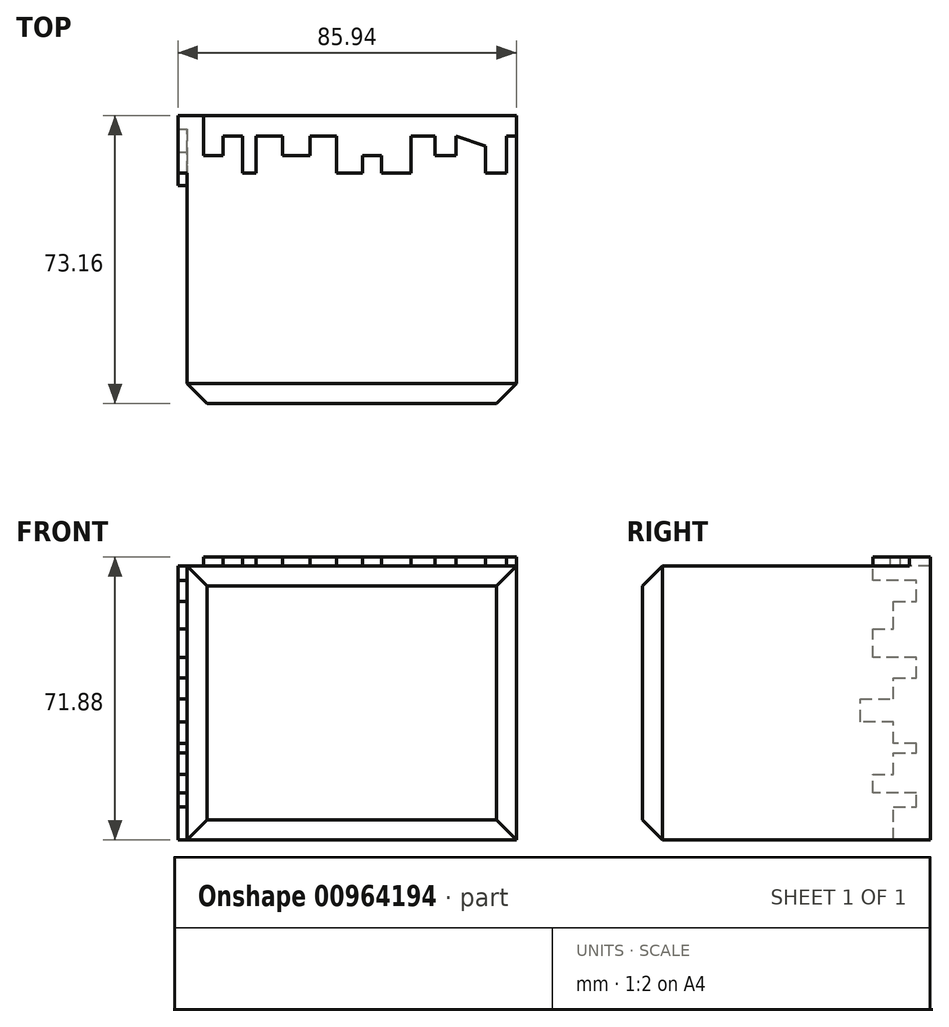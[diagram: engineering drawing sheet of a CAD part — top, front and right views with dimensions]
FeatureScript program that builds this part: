
annotation { "Feature Type Name" : "Feature", "Feature Type Description" : "" }
export const myFeature = defineFeature(function(context is Context, id is Id, definition is map)
    precondition{}
    {
        {
            var Q0;
            Q0=qCreatedBy(makeId("Top.planeOp"),FACE);
            var sketch = newSketch(context, id + "F0", { "sketchPlane" : qUnion([Q0])});
            skLineSegment(sketch, "E0.bottom", {"start": v(-44.6, 47.36) * mm, "end": v(39.06, 47.36) * mm});
            skLineSegment(sketch, "E0.top", {"start": v(-44.6, -25.8) * mm, "end": v(39.06, -25.8) * mm});
            skLineSegment(sketch, "E0.left", {"start": v(-44.6, 47.36) * mm, "end": v(-44.6, -25.8) * mm});
            skLineSegment(sketch, "E0.right", {"start": v(39.06, 47.36) * mm, "end": v(39.06, -25.8) * mm});
            skSolve(sketch);
        }
        {
            var Q0;
            Q0=makeQuery(id+"F0.imprint","IMPRINT",FACE,{"disambiguationData":[TD([[makeQuery(id+"F0.imprint","IMPRINT",EDGE,{"derivedFrom":sQuery(id+"F0.wireOp",EDGE,"E0.bottom")}),-1.0]])]});
            extrude(context, id + "F1", {"entities" : qUnion([Q0]), "depth" : 69.6 * mm});
        }
        {
            var Q0;
            Q0=makeQuery(id+"F1.opExtrude","SWEPT_FACE",FACE,{"disambiguationData":[OSD([sQuery(id+"F0.wireOp",EDGE,"E0.left")])]});
            var sketch = newSketch(context, id + "F2", { "sketchPlane" : qUnion([Q0])});
            skLineSegment(sketch, "E1", {"start": v(-38.04, 0) * mm, "end": v(-38.04, 8.45) * mm});
            skLineSegment(sketch, "E2", {"start": v(-38.04, 8.45) * mm, "end": v(-43.87, 8.45) * mm});
            skLineSegment(sketch, "E3", {"start": v(-43.87, 8.45) * mm, "end": v(-43.87, 11.95) * mm});
            skLineSegment(sketch, "E4", {"start": v(-43.87, 11.95) * mm, "end": v(-32.8, 11.95) * mm});
            skLineSegment(sketch, "E5", {"start": v(-32.8, 11.95) * mm, "end": v(-32.8, 16.61) * mm});
            skLineSegment(sketch, "E6", {"start": v(-32.8, 16.61) * mm, "end": v(-38.04, 16.61) * mm});
            skLineSegment(sketch, "E7", {"start": v(-38.04, 16.61) * mm, "end": v(-38.04, 22.15) * mm});
            skLineSegment(sketch, "E8", {"start": v(-38.04, 22.15) * mm, "end": v(-43.87, 22.15) * mm});
            skLineSegment(sketch, "E9", {"start": v(-43.87, 22.15) * mm, "end": v(-43.87, 24.48) * mm});
            skLineSegment(sketch, "E10", {"start": v(-43.87, 24.48) * mm, "end": v(-38.04, 24.48) * mm});
            skLineSegment(sketch, "E11", {"start": v(-38.04, 24.48) * mm, "end": v(-38.04, 30.02) * mm});
            skLineSegment(sketch, "E12", {"start": v(-38.04, 30.02) * mm, "end": v(-29.58, 30.02) * mm});
            skLineSegment(sketch, "E13", {"start": v(-29.58, 30.02) * mm, "end": v(-29.58, 35.85) * mm});
            skLineSegment(sketch, "E14", {"start": v(-29.58, 35.85) * mm, "end": v(-38.04, 35.85) * mm});
            skLineSegment(sketch, "E15", {"start": v(-38.04, 35.85) * mm, "end": v(-38.04, 41.1) * mm});
            skLineSegment(sketch, "E16", {"start": v(-38.04, 41.1) * mm, "end": v(-43.87, 41.1) * mm});
            skLineSegment(sketch, "E17", {"start": v(-43.87, 41.1) * mm, "end": v(-43.87, 46.34) * mm});
            skLineSegment(sketch, "E18", {"start": v(-43.87, 46.34) * mm, "end": v(-32.8, 46.34) * mm});
            skLineSegment(sketch, "E19", {"start": v(-32.8, 46.34) * mm, "end": v(-32.8, 53.63) * mm});
            skLineSegment(sketch, "E20", {"start": v(-32.8, 53.63) * mm, "end": v(-38.04, 53.63) * mm});
            skLineSegment(sketch, "E21", {"start": v(-38.04, 53.63) * mm, "end": v(-38.04, 60.63) * mm});
            skLineSegment(sketch, "E22", {"start": v(-38.04, 60.63) * mm, "end": v(-43.87, 60.63) * mm});
            skLineSegment(sketch, "E23", {"start": v(-43.87, 60.63) * mm, "end": v(-43.87, 65.87) * mm});
            skLineSegment(sketch, "E24", {"start": v(-43.87, 65.87) * mm, "end": v(-32.8, 65.87) * mm});
            skLineSegment(sketch, "E25", {"start": v(-32.8, 65.87) * mm, "end": v(-32.8, 69.6) * mm});
            skLineSegment(sketch, "E26", {"start": v(-32.8, 69.6) * mm, "end": v(-47.36, 69.6) * mm});
            skLineSegment(sketch, "E27", {"start": v(-47.36, 69.6) * mm, "end": v(-47.36, 0) * mm});
            skLineSegment(sketch, "E28", {"start": v(-47.36, 0) * mm, "end": v(-38.04, 0) * mm});
            skSolve(sketch);
        }
        {
            var Q0;
            Q0=makeQuery(id+"F2.imprint","IMPRINT",FACE,{"disambiguationData":[TD([[makeQuery(id+"F2.imprint","IMPRINT",EDGE,{"derivedFrom":sQuery(id+"F2.wireOp",EDGE,"E1")}),1.0]])]});
            extrude(context, id + "F3", {"entities" : qUnion([Q0]), "operationType" : NewBodyOperationType.ADD, "depth" : 2.3 * mm});
        }
        {
            var Q0;
            Q0=makeQuery(id+"F3.boolean.opBoolean","MERGE",FACE,{"derivedFrom":[makeQuery(id+"F1.opExtrude","CAP_FACE",FACE,{"disambiguationData":[OSD([sQuery(id+"F0.wireOp",EDGE,"E0.bottom"),sQuery(id+"F0.wireOp",EDGE,"E0.top"),sQuery(id+"F0.wireOp",EDGE,"E0.left"),sQuery(id+"F0.wireOp",EDGE,"E0.right")])],"isStart":false}),makeQuery(id+"F3.opExtrude","SWEPT_FACE",FACE,{"disambiguationData":[OSD([sQuery(id+"F2.wireOp",EDGE,"E26")])]})]});
            var sketch = newSketch(context, id + "F4", { "sketchPlane" : qUnion([Q0])});
            skLineSegment(sketch, "E29", {"start": v(-40.41, 47.36) * mm, "end": v(-40.41, 37.16) * mm});
            skLineSegment(sketch, "E30", {"start": v(-40.41, 37.16) * mm, "end": v(-35.46, 37.16) * mm});
            skLineSegment(sketch, "E31", {"start": v(-35.46, 37.16) * mm, "end": v(-35.46, 42.12) * mm});
            skLineSegment(sketch, "E32", {"start": v(-35.46, 42.12) * mm, "end": v(-30.5, 42.12) * mm});
            skLineSegment(sketch, "E33", {"start": v(-30.5, 42.12) * mm, "end": v(-30.5, 32.8) * mm});
            skLineSegment(sketch, "E34", {"start": v(-30.5, 32.8) * mm, "end": v(-27, 32.8) * mm});
            skLineSegment(sketch, "E35", {"start": v(-27, 32.8) * mm, "end": v(-27, 42.12) * mm});
            skLineSegment(sketch, "E36", {"start": v(-27, 42.12) * mm, "end": v(-20.3, 42.12) * mm});
            skLineSegment(sketch, "E37", {"start": v(-20.3, 42.12) * mm, "end": v(-20.3, 37.16) * mm});
            skLineSegment(sketch, "E38", {"start": v(-20.3, 37.16) * mm, "end": v(-13.3, 37.16) * mm});
            skLineSegment(sketch, "E39", {"start": v(-13.3, 37.16) * mm, "end": v(-13.3, 42.12) * mm});
            skLineSegment(sketch, "E40", {"start": v(-13.3, 42.12) * mm, "end": v(-6.6, 42.12) * mm});
            skLineSegment(sketch, "E41", {"start": v(-6.6, 42.12) * mm, "end": v(-6.6, 32.8) * mm});
            skLineSegment(sketch, "E42", {"start": v(-6.6, 32.8) * mm, "end": v(0, 32.8) * mm});
            skLineSegment(sketch, "E43", {"start": v(0, 32.8) * mm, "end": v(0, 37.16) * mm});
            skLineSegment(sketch, "E44", {"start": v(0, 37.16) * mm, "end": v(4.77, 37.16) * mm});
            skLineSegment(sketch, "E45", {"start": v(4.77, 37.16) * mm, "end": v(4.77, 32.8) * mm});
            skLineSegment(sketch, "E46", {"start": v(4.77, 32.8) * mm, "end": v(12.35, 32.8) * mm});
            skLineSegment(sketch, "E47", {"start": v(12.35, 32.8) * mm, "end": v(12.35, 42.12) * mm});
            skLineSegment(sketch, "E48", {"start": v(12.35, 42.12) * mm, "end": v(18.47, 42.12) * mm});
            skLineSegment(sketch, "E49", {"start": v(18.47, 42.12) * mm, "end": v(18.47, 37.16) * mm});
            skLineSegment(sketch, "E50", {"start": v(18.47, 37.16) * mm, "end": v(23.71, 37.16) * mm});
            skLineSegment(sketch, "E51", {"start": v(23.71, 37.16) * mm, "end": v(23.71, 42.12) * mm});
            skLineSegment(sketch, "E52", {"start": v(23.71, 42.12) * mm, "end": v(31.3, 39.64) * mm});
            skPoint(sketch, "E52.endSnap0", {"position": v(23.71, 39.64) * mm});
            skLineSegment(sketch, "E53", {"start": v(31.3, 39.64) * mm, "end": v(31.3, 32.8) * mm});
            skLineSegment(sketch, "E54", {"start": v(31.3, 32.8) * mm, "end": v(36.54, 32.8) * mm});
            skLineSegment(sketch, "E55", {"start": v(36.54, 32.8) * mm, "end": v(36.54, 42.12) * mm});
            skLineSegment(sketch, "E56", {"start": v(36.54, 42.12) * mm, "end": v(39.06, 42.12) * mm});
            skLineSegment(sketch, "E57", {"start": v(39.06, 42.12) * mm, "end": v(39.06, 47.36) * mm});
            skLineSegment(sketch, "E58", {"start": v(39.06, 47.36) * mm, "end": v(-46.88, 47.36) * mm});
            skLineSegment(sketch, "E59", {"start": v(-46.88, 47.36) * mm, "end": v(-46.88, 37.16) * mm});
            skLineSegment(sketch, "E60", {"start": v(-46.88, 37.16) * mm, "end": v(-40.41, 37.16) * mm});
            skSolve(sketch);
        }
        {
            var Q0;
            {var subQ0=sQuery(id+"F4.wireOp",EDGE,"E29");Q0=makeQuery(id+"F4.imprint","IMPRINT",FACE,{"disambiguationData":[TD([[makeQuery(id+"F4.imprint","IMPRINT",EDGE,{"derivedFrom":subQ0}),1.0]])]});}
            extrude(context, id + "F5", {"entities" : qUnion([Q0]), "operationType" : NewBodyOperationType.ADD, "depth" : 2.3 * mm});
        }
        {
            var Q0;
            Q0=makeQuery(id+"F1.opExtrude","CAP_EDGE",EDGE,{"disambiguationData":[OSD([sQuery(id+"F0.wireOp",EDGE,"E0.top")])],"isStart":false});
            var Q1;
            Q1=makeQuery(id+"F1.opExtrude","SWEPT_EDGE",EDGE,{"disambiguationData":[OSD([sQuery(id+"F0.wireOp",EDGE,"E0.top"),sQuery(id+"F0.wireOp",EDGE,"E0.left")])]});
            var Q2;
            Q2=makeQuery(id+"F1.opExtrude","CAP_EDGE",EDGE,{"disambiguationData":[OSD([sQuery(id+"F0.wireOp",EDGE,"E0.top")])],"isStart":true});
            var Q3;
            Q3=makeQuery(id+"F1.opExtrude","SWEPT_EDGE",EDGE,{"disambiguationData":[OSD([sQuery(id+"F0.wireOp",EDGE,"E0.top"),sQuery(id+"F0.wireOp",EDGE,"E0.right")])]});
            chamfer(context, id + "F6", {"entities" : qUnion([Q0, Q1, Q2, Q3]), "width" : 5.08 * mm, "tangentPropagation" : true});
        }
    });
